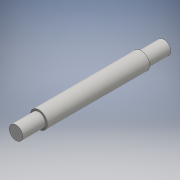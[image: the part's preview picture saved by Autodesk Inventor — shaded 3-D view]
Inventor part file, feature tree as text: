
AUTODESK INVENTOR PART (.ipt)
format: ipt  version: 2016 (Build 200138000, 138)  size: 102,912 bytes
history: native  units: mm
features: extrude x3, sketch x3, other x1
ambient origin geometry x8: Origin, YZ Plane, XZ Plane, XY Plane, X Axis, Y Axis, Z Axis, Center Point
bodies: Body1 (feature_tree)
feature tree (7):
  other  "ソリッド1"
  extrude  "押し出し1"  Depth=15.0mm
  extrude  "押し出し2"  Depth=110.0mm TaperAngle=0.0deg
  extrude  "押し出し3"  Depth=12.0mm
  sketch  "スケッチ1"
  sketch  "スケッチ2"
  sketch  "スケッチ3"
